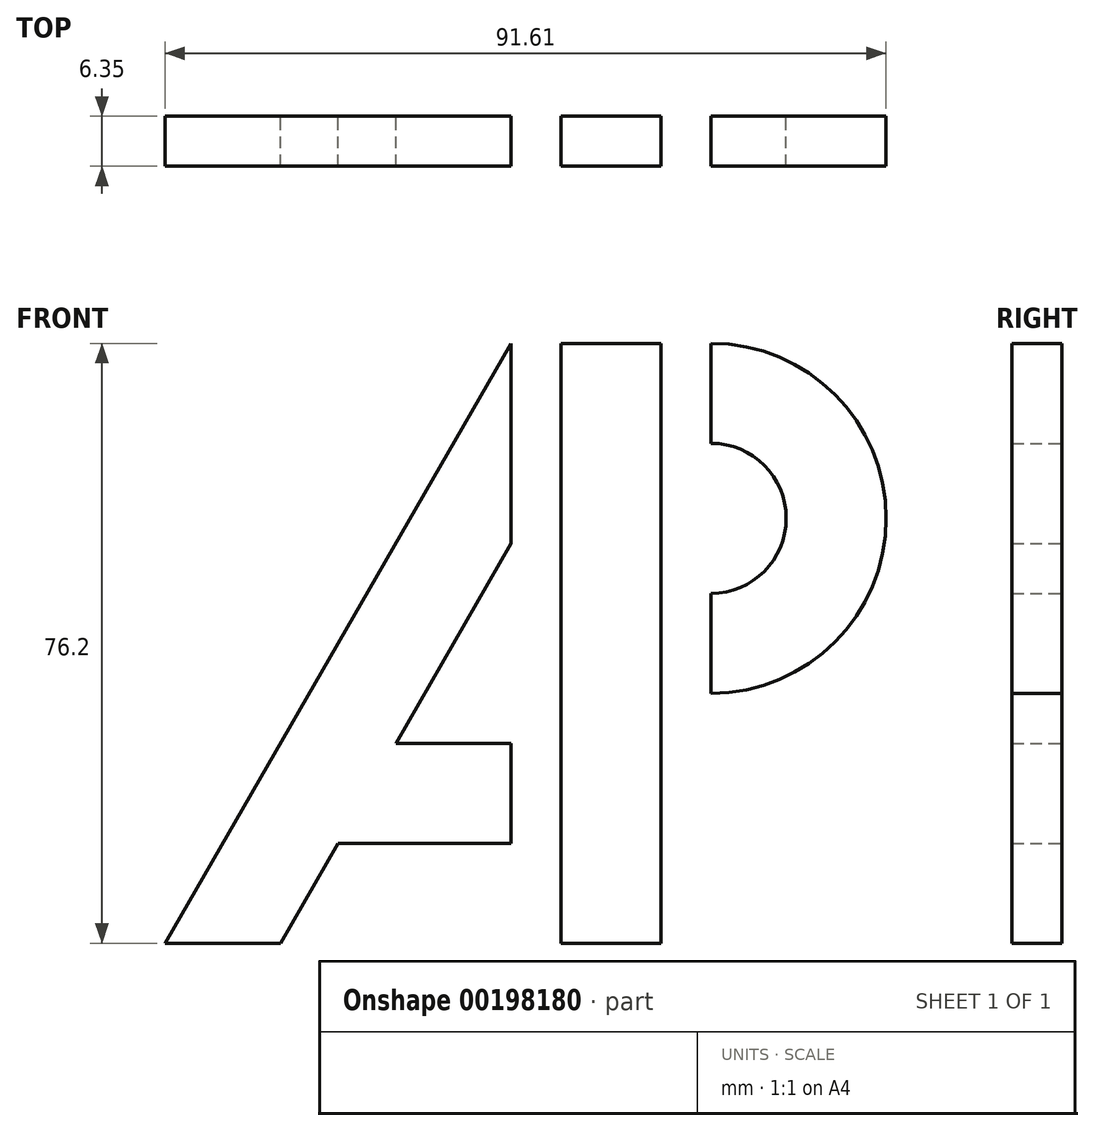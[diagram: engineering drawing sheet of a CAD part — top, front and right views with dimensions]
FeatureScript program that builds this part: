
annotation { "Feature Type Name" : "Feature", "Feature Type Description" : "" }
export const myFeature = defineFeature(function(context is Context, id is Id, definition is map)
    precondition{}
    {
        {
            var Q0;
            Q0=qCreatedBy(makeId("Front.planeOp"),FACE);
            var sketch = newSketch(context, id + "F0", { "sketchPlane" : qUnion([Q0])});
            skLineSegment(sketch, "E0.bottom", {"start": v(-6.35, 38.1) * mm, "end": v(6.35, 38.1) * mm});
            skLineSegment(sketch, "E0.top", {"start": v(-6.35, -38.1) * mm, "end": v(6.35, -38.1) * mm});
            skLineSegment(sketch, "E0.left", {"start": v(-6.35, 38.1) * mm, "end": v(-6.35, -38.1) * mm});
            skLineSegment(sketch, "E0.right", {"start": v(6.35, 38.1) * mm, "end": v(6.35, -38.1) * mm});
            skPoint(sketch, "E0.middle", {"position": v(0, 0) * mm});
            skLineSegment(sketch, "E1.bottom", {"start": v(6.35, 38.1) * mm, "end": v(12.7, 38.1) * mm});
            skLineSegment(sketch, "E1.top", {"start": v(6.35, 25.4) * mm, "end": v(12.7, 25.4) * mm});
            skLineSegment(sketch, "E1.left", {"start": v(6.35, 38.1) * mm, "end": v(6.35, 25.4) * mm});
            skLineSegment(sketch, "E1.right", {"start": v(12.7, 38.1) * mm, "end": v(12.7, 25.4) * mm});
            skLineSegment(sketch, "E2.bottom", {"start": v(6.35, 6.35) * mm, "end": v(12.7, 6.35) * mm});
            skLineSegment(sketch, "E2.top", {"start": v(6.35, -6.35) * mm, "end": v(12.7, -6.35) * mm});
            skLineSegment(sketch, "E2.left", {"start": v(6.35, 6.35) * mm, "end": v(6.35, -6.35) * mm});
            skLineSegment(sketch, "E2.right", {"start": v(12.7, 6.35) * mm, "end": v(12.7, -6.35) * mm});
            skLineSegment(sketch, "E3.bottom", {"start": v(-6.35, 38.1) * mm, "end": v(-12.7, 38.1) * mm});
            skLineSegment(sketch, "E3.top", {"start": v(-6.35, 12.7) * mm, "end": v(-12.7, 12.7) * mm});
            skLineSegment(sketch, "E3.left", {"start": v(-6.35, 38.1) * mm, "end": v(-6.35, 12.7) * mm});
            skLineSegment(sketch, "E3.right", {"start": v(-12.7, 38.1) * mm, "end": v(-12.7, 12.7) * mm});
            skLineSegment(sketch, "E4.bottom", {"start": v(-6.35, -38.1) * mm, "end": v(-12.7, -38.1) * mm});
            skLineSegment(sketch, "E4.top", {"start": v(-6.35, -25.4) * mm, "end": v(-12.7, -25.4) * mm});
            skLineSegment(sketch, "E4.left", {"start": v(-6.35, -38.1) * mm, "end": v(-6.35, -25.4) * mm});
            skLineSegment(sketch, "E4.right", {"start": v(-12.7, -38.1) * mm, "end": v(-12.7, -25.4) * mm});
            skArc(sketch, "E5", {"start": v(12.7, 6.35) * mm, "mid": v(22.22, 15.87) * mm, "end": v(12.7, 25.4) * mm});
            skArc(sketch, "E6", {"start": v(12.7, -6.35) * mm, "mid": v(34.92, 15.87) * mm, "end": v(12.7, 38.1) * mm});
            skLineSegment(sketch, "E7", {"start": v(-12.7, -38.1) * mm, "end": v(-56.7, -38.1) * mm});
            skLineSegment(sketch, "E8", {"start": v(-56.7, -38.1) * mm, "end": v(-12.7, 38.1) * mm});
            skLineSegment(sketch, "E9", {"start": v(-12.7, 12.7) * mm, "end": v(-34.7, -25.4) * mm});
            skLineSegment(sketch, "E10", {"start": v(-34.7, -25.4) * mm, "end": v(-12.7, -25.4) * mm});
            skLineSegment(sketch, "E11", {"start": v(-12.7, -25.4) * mm, "end": v(-12.7, -12.7) * mm});
            skLineSegment(sketch, "E12", {"start": v(-12.7, -12.7) * mm, "end": v(-6.35, -12.7) * mm});
            skLineSegment(sketch, "E13", {"start": v(-12.7, -12.7) * mm, "end": v(-27.36, -12.7) * mm});
            skLineSegment(sketch, "E14", {"start": v(-34.7, -25.4) * mm, "end": v(-42.03, -38.1) * mm});
            skSolve(sketch);
        }
        {
            var Q0;
            Q0=makeQuery(id+"F0.imprint","IMPRINT",FACE,{"disambiguationData":[TD([[makeQuery(id+"F0.imprint","IMPRINT",EDGE,{"derivedFrom":sQuery(id+"F0.wireOp",EDGE,"E3.right")}),-1.0]])]});
            var Q1;
            Q1=makeQuery(id+"F0.imprint","IMPRINT",FACE,{"disambiguationData":[TD([[makeQuery(id+"F0.imprint","IMPRINT",EDGE,{"derivedFrom":sQuery(id+"F0.wireOp",EDGE,"E0.bottom")}),-1.0]])]});
            var Q2;
            Q2=makeQuery(id+"F0.imprint","IMPRINT",FACE,{"disambiguationData":[TD([[makeQuery(id+"F0.imprint","IMPRINT",EDGE,{"derivedFrom":sQuery(id+"F0.wireOp",EDGE,"E1.right")}),1.0]])]});
            var Q3;
            {var subQ0=sQuery(id+"F0.wireOp",EDGE,"E10");Q3=makeQuery(id+"F0.imprint","IMPRINT",FACE,{"disambiguationData":[TD([[makeQuery(id+"F0.imprint","IMPRINT",EDGE,{"derivedFrom":subQ0}),1.0]])]});}
            extrude(context, id + "F1", {"entities" : qUnion([Q0, Q1, Q2, Q3]), "depth" : 6.35 * mm});
        }
    });
